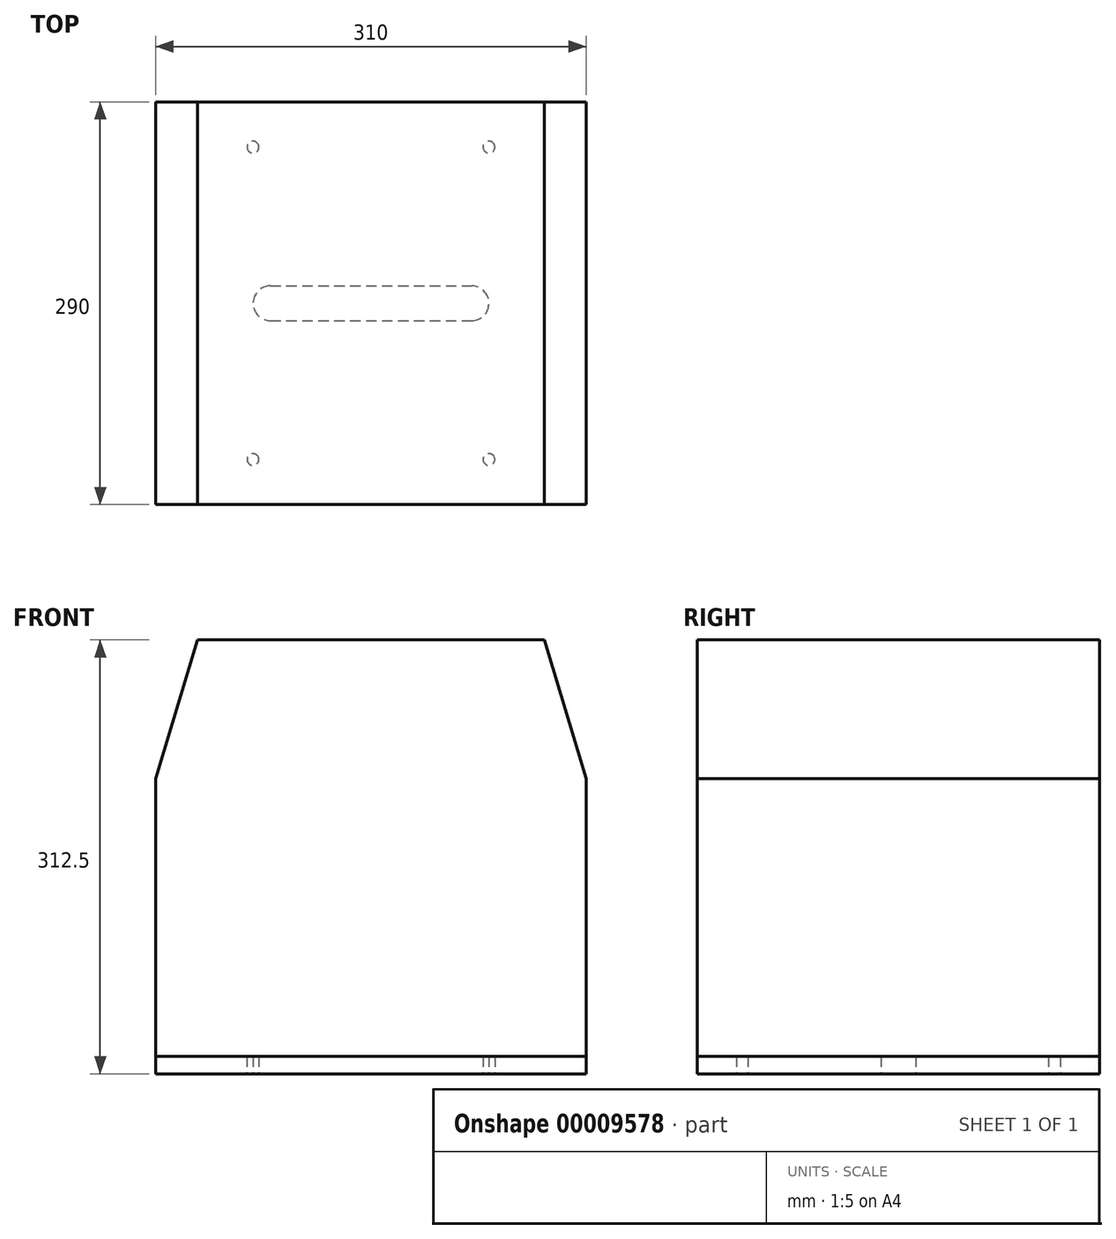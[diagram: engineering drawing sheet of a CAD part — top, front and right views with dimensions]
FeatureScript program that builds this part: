
annotation { "Feature Type Name" : "Feature", "Feature Type Description" : "" }
export const myFeature = defineFeature(function(context is Context, id is Id, definition is map)
    precondition{}
    {
        {
            var Q0;
            Q0=qCreatedBy(makeId("Top.planeOp"),FACE);
            var sketch = newSketch(context, id + "F0", { "sketchPlane" : qUnion([Q0])});
            skLineSegment(sketch, "E0.rect.bottom", {"start": v(-155, 145) * mm, "end": v(155, 145) * mm});
            skLineSegment(sketch, "E0.rect.top", {"start": v(-155, -145) * mm, "end": v(155, -145) * mm});
            skLineSegment(sketch, "E0.rect.left", {"start": v(-155, 145) * mm, "end": v(-155, -145) * mm});
            skLineSegment(sketch, "E0.rect.right", {"start": v(155, 145) * mm, "end": v(155, -145) * mm});
            skPoint(sketch, "E0.rect.middle", {"position": v(0, 0) * mm});
            skLineSegment(sketch, "E1.rect.bottom", {"start": v(-85, 112.5) * mm, "end": v(85, 112.5) * mm, "construction": true});
            skLineSegment(sketch, "E1.rect.top", {"start": v(-85, -112.5) * mm, "end": v(85, -112.5) * mm, "construction": true});
            skLineSegment(sketch, "E1.rect.left", {"start": v(-85, 112.5) * mm, "end": v(-85, -112.5) * mm, "construction": true});
            skLineSegment(sketch, "E1.rect.right", {"start": v(85, 112.5) * mm, "end": v(85, -112.5) * mm, "construction": true});
            skCircle(sketch, "E2", {"center": v(-85, 112.5) * mm, "radius": 4.25 * mm});
            skCircle(sketch, "E3", {"center": v(85, 112.5) * mm, "radius": 4.25 * mm});
            skCircle(sketch, "E4", {"center": v(85, -112.5) * mm, "radius": 4.25 * mm});
            skCircle(sketch, "E5", {"center": v(-85, -112.5) * mm, "radius": 4.25 * mm});
            skLineSegment(sketch, "E6.0", {"start": v(-72.5, 112.5) * mm, "end": v(-72.5, -112.5) * mm, "construction": true});
            skLineSegment(sketch, "E7", {"start": v(0, 0) * mm, "end": v(0, -160.07) * mm, "construction": true});
            skLineSegment(sketch, "E8", {"start": v(0, 0) * mm, "end": v(-72.5, 0) * mm, "construction": true});
            skArc(sketch, "E9", {"start": v(-72.5, 12.5) * mm, "mid": v(-85, 0) * mm, "end": v(-72.5, -12.5) * mm});
            skArc(sketch, "E10.0.MirrorC", {"start": v(72.5, 12.5) * mm, "mid": v(85, 0) * mm, "end": v(72.5, -12.5) * mm});
            skLineSegment(sketch, "E11", {"start": v(-72.5, 12.5) * mm, "end": v(72.5, 12.5) * mm});
            skLineSegment(sketch, "E12", {"start": v(-72.5, -12.5) * mm, "end": v(72.5, -12.5) * mm});
            skSolve(sketch);
        }
        {
            var Q0;
            Q0 = qSketchRegion(id + "F0", true);
            extrude(context, id + "F1", {"entities" : qUnion([Q0]), "depth" : 12.5 * mm});
        }
        {
            var Q0;
            Q0=makeQuery(id+"F1.opExtrude","CAP_FACE",FACE,{"disambiguationData":[OSD([sQuery(id+"F0.wireOp",EDGE,"E0.rect.bottom"),sQuery(id+"F0.wireOp",EDGE,"E0.rect.top"),sQuery(id+"F0.wireOp",EDGE,"E0.rect.left"),sQuery(id+"F0.wireOp",EDGE,"E0.rect.right"),sQuery(id+"F0.wireOp",EDGE,"E2"),sQuery(id+"F0.wireOp",EDGE,"E3"),sQuery(id+"F0.wireOp",EDGE,"E4"),sQuery(id+"F0.wireOp",EDGE,"E5"),sQuery(id+"F0.wireOp",EDGE,"E9"),sQuery(id+"F0.wireOp",EDGE,"E10.0.MirrorC"),sQuery(id+"F0.wireOp",EDGE,"E11"),sQuery(id+"F0.wireOp",EDGE,"E12")])],"isStart":false});
            var sketch = newSketch(context, id + "F2", { "sketchPlane" : qUnion([Q0])});
            skLineSegment(sketch, "E13.0", {"start": v(-155, 145) * mm, "end": v(155, 145) * mm});
            skLineSegment(sketch, "E14.0", {"start": v(155, 145) * mm, "end": v(155, -145) * mm});
            skLineSegment(sketch, "E15.0", {"start": v(-155, -145) * mm, "end": v(155, -145) * mm});
            skLineSegment(sketch, "E16.0", {"start": v(-155, 145) * mm, "end": v(-155, -145) * mm});
            skSolve(sketch);
        }
        {
            var Q0;
            Q0 = qSketchRegion(id + "F2", true);
            extrude(context, id + "F3", {"entities" : qUnion([Q0]), "depth" : 300 * mm});
        }
        {
            var Q0;
            Q0=makeQuery(id+"F3.opExtrude","CAP_EDGE",EDGE,{"disambiguationData":[OSD([sQuery(id+"F2.wireOp",EDGE,"E16.0")])],"isStart":false});
            var Q1;
            Q1=makeQuery(id+"F3.opExtrude","CAP_EDGE",EDGE,{"disambiguationData":[OSD([sQuery(id+"F2.wireOp",EDGE,"E14.0")])],"isStart":false});
            chamfer(context, id + "F4", {"entities" : qUnion([Q0, Q1]), "chamferType" : ChamferType.TWO_OFFSETS, "width1" : 30 * mm, "oppositeDirection" : false, "width2" : 100 * mm, "tangentPropagation" : true});
        }
    });
